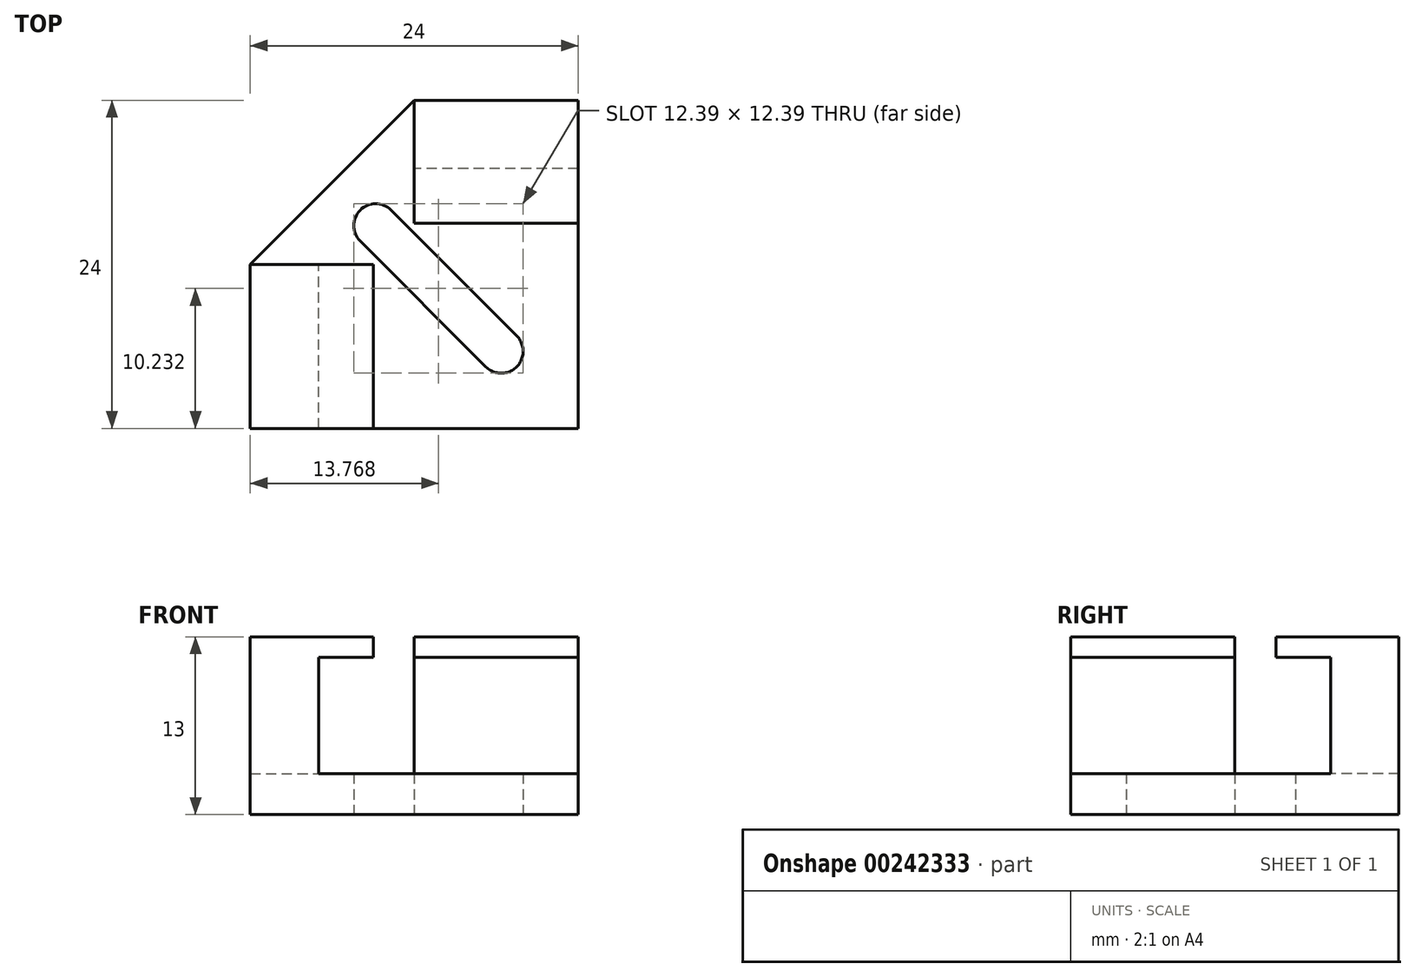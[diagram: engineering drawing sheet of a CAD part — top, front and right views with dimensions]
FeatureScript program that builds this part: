
annotation { "Feature Type Name" : "Feature", "Feature Type Description" : "" }
export const myFeature = defineFeature(function(context is Context, id is Id, definition is map)
    precondition{}
    {
        {
            var Q0;
            Q0=qCreatedBy(makeId("Top.planeOp"),FACE);
            var sketch = newSketch(context, id + "F0", { "sketchPlane" : qUnion([Q0])});
            skLineSegment(sketch, "E0.bottom", {"start": v(0, 12) * mm, "end": v(12, 12) * mm});
            skLineSegment(sketch, "E0.top", {"start": v(-12, -12) * mm, "end": v(12, -12) * mm});
            skLineSegment(sketch, "E0.left", {"start": v(-12, 0) * mm, "end": v(-12, -12) * mm});
            skLineSegment(sketch, "E0.right", {"start": v(12, 12) * mm, "end": v(12, -12) * mm});
            skPoint(sketch, "E1", {"position": v(0, 0) * mm});
            skPoint(sketch, "E1.positionSnap0", {"position": v(0, 12) * mm});
            skPoint(sketch, "E1.positionSnap1", {"position": v(-12, 0) * mm});
            skLineSegment(sketch, "E2", {"start": v(-12, 12) * mm, "end": v(12, -12) * mm, "construction": true});
            skArc(sketch, "E3", {"start": v(-1.7, 3.96) * mm, "mid": v(-3.96, 3.96) * mm, "end": v(-3.96, 1.7) * mm});
            skArc(sketch, "E4", {"start": v(5.23, -7.5) * mm, "mid": v(7.5, -7.5) * mm, "end": v(7.5, -5.23) * mm});
            skLineSegment(sketch, "E5", {"start": v(-3.96, 1.7) * mm, "end": v(5.23, -7.5) * mm});
            skLineSegment(sketch, "E6", {"start": v(-1.7, 3.96) * mm, "end": v(7.5, -5.23) * mm});
            skLineSegment(sketch, "E7", {"start": v(-7, -12) * mm, "end": v(-7, 0) * mm});
            skLineSegment(sketch, "E8", {"start": v(12, 7) * mm, "end": v(0, 7) * mm});
            skLineSegment(sketch, "E9", {"start": v(0, 12) * mm, "end": v(0, 7) * mm});
            skLineSegment(sketch, "E10", {"start": v(-12, 0) * mm, "end": v(-7, 0) * mm});
            skLineSegment(sketch, "E11", {"start": v(0, 12) * mm, "end": v(-12, 0) * mm});
            skSolve(sketch);
        }
        {
            var Q0;
            Q0=makeQuery(id+"F0.imprint","IMPRINT",FACE,{"disambiguationData":[TD([[makeQuery(id+"F0.imprint","IMPRINT",EDGE,{"derivedFrom":sQuery(id+"F0.wireOp",EDGE,"E3")}),-1.0]])]});
            extrude(context, id + "F1", {"entities" : qUnion([Q0]), "depth" : 3 * mm});
        }
        {
            var Q0;
            {var subQ3=sQuery(id+"F0.wireOp",EDGE,"E7");Q0=makeQuery(id+"F0.imprint","IMPRINT",FACE,{"disambiguationData":[TD([[makeQuery(id+"F0.imprint","IMPRINT",EDGE,{"derivedFrom":subQ3}),1.0]])]});}
            var Q1;
            {var subQ4=sQuery(id+"F0.wireOp",EDGE,"E8");Q1=makeQuery(id+"F0.imprint","IMPRINT",FACE,{"disambiguationData":[TD([[makeQuery(id+"F0.imprint","IMPRINT",EDGE,{"derivedFrom":subQ4}),-1.0]])]});}
            extrude(context, id + "F2", {"entities" : qUnion([Q0, Q1]), "operationType" : NewBodyOperationType.ADD, "depth" : 13 * mm});
        }
        {
            var Q0;
            Q0=makeQuery(id+"F2.opExtrude","CAP_FACE",FACE,{"disambiguationData":[OSD([sQuery(id+"F0.wireOp",EDGE,"E0.top"),sQuery(id+"F0.wireOp",EDGE,"E0.left"),sQuery(id+"F0.wireOp",EDGE,"E7"),sQuery(id+"F0.wireOp",EDGE,"E10")])],"isStart":false});
            cPlane(context, id + "F3", {"entities" : qUnion([Q0]), "cplaneType" : CPlaneType.OFFSET, "offset" : 0 * mm, "width" : 150 * mm, "height" : 150 * mm});
        }
        {
            var Q0;
            Q0=qCreatedBy(id+"F3.planeOp",FACE);
            var sketch = newSketch(context, id + "F4", { "sketchPlane" : qUnion([Q0])});
            skLineSegment(sketch, "E12.0", {"start": v(-7, -12) * mm, "end": v(-7, 0) * mm});
            skLineSegment(sketch, "E12.1", {"start": v(12, 7) * mm, "end": v(0, 7) * mm});
            skLineSegment(sketch, "E13", {"start": v(-3, 0) * mm, "end": v(-3, -12) * mm});
            skLineSegment(sketch, "E14", {"start": v(0, 7) * mm, "end": v(0, 3) * mm});
            skLineSegment(sketch, "E15", {"start": v(0, 3) * mm, "end": v(12, 3) * mm});
            skLineSegment(sketch, "E16", {"start": v(12, 3) * mm, "end": v(12, 7) * mm});
            skLineSegment(sketch, "E17", {"start": v(-7, 0) * mm, "end": v(-3, 0) * mm});
            skLineSegment(sketch, "E18", {"start": v(-7, -12) * mm, "end": v(-3, -12) * mm});
            skSolve(sketch);
        }
        {
            var Q0;
            Q0=makeQuery(id+"F4.imprint","IMPRINT",FACE,{"disambiguationData":[TD([[makeQuery(id+"F4.imprint","IMPRINT",EDGE,{"derivedFrom":sQuery(id+"F4.wireOp",EDGE,"E12.0")}),-1.0]])]});
            var Q1;
            Q1=makeQuery(id+"F4.imprint","IMPRINT",FACE,{"disambiguationData":[TD([[makeQuery(id+"F4.imprint","IMPRINT",EDGE,{"derivedFrom":sQuery(id+"F4.wireOp",EDGE,"E12.1")}),1.0]])]});
            extrude(context, id + "F5", {"entities" : qUnion([Q0, Q1]), "operationType" : NewBodyOperationType.ADD, "oppositeDirection" : true, "depth" : 1.5 * mm});
        }
    });
